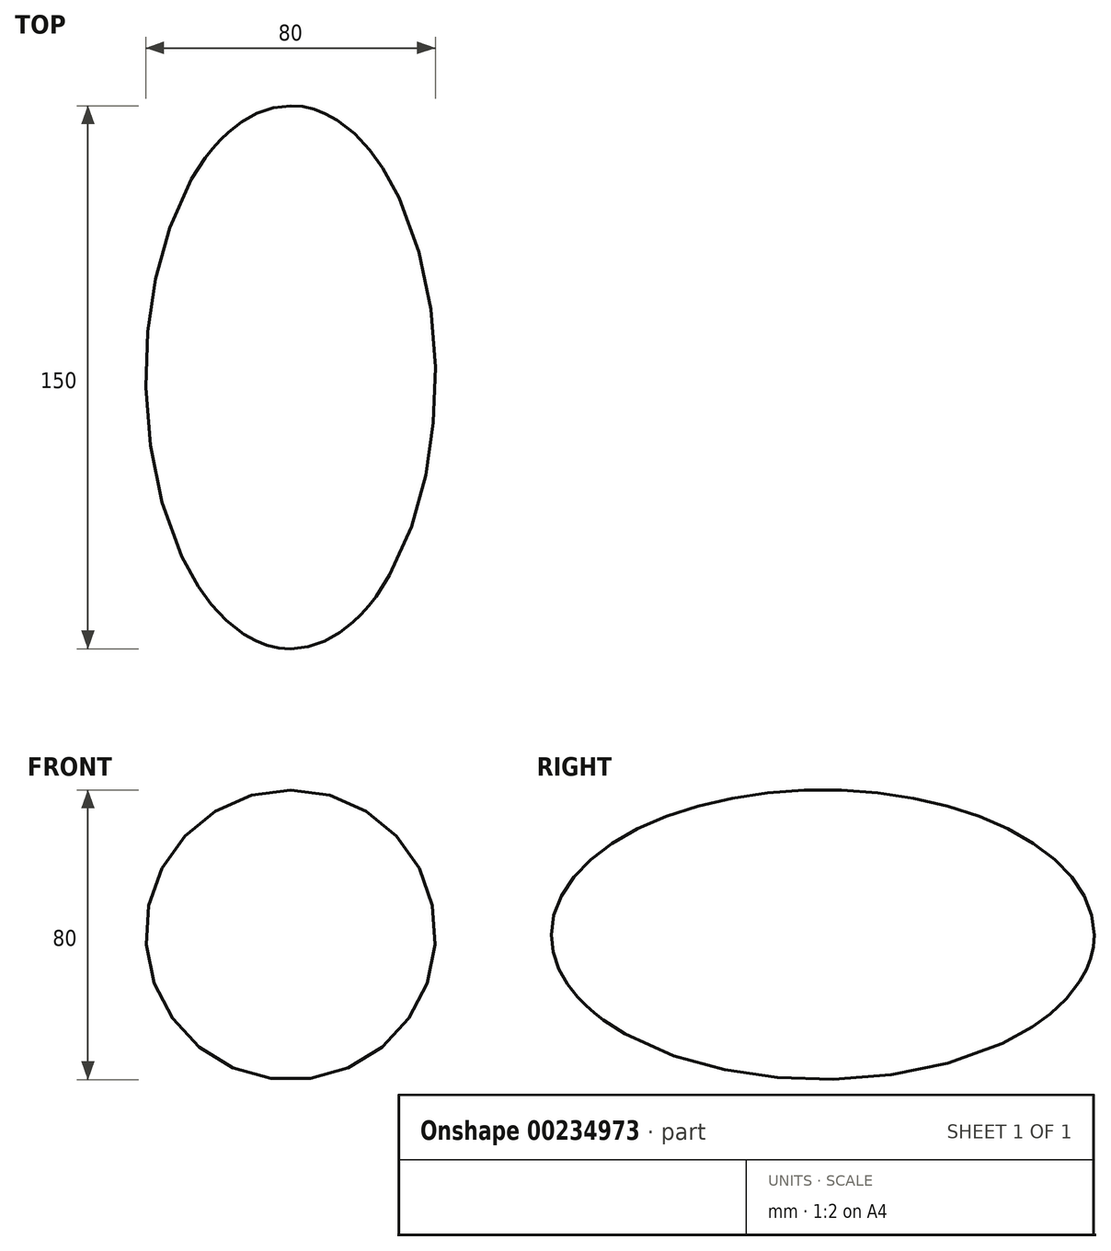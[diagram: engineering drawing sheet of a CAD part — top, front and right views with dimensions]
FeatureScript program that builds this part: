
annotation { "Feature Type Name" : "Feature", "Feature Type Description" : "" }
export const myFeature = defineFeature(function(context is Context, id is Id, definition is map)
    precondition{}
    {
        {
            var Q0;
            Q0=qCreatedBy(makeId("Right.planeOp"),FACE);
            var sketch = newSketch(context, id + "F0", { "sketchPlane" : qUnion([Q0])});
            skEllipticalArc(sketch, "E0", {});
            skLineSegment(sketch, "E1", {"start": v(75, 0) * mm, "end": v(-75, 0) * mm});
            const initialGuessF0  = {"E0": [0, 0, 1, 0, 0.075, 0.04, 0, 3.141592653589793]};
            skSetInitialGuess(sketch, initialGuessF0);
            skSolve(sketch);
        }
        {
            var Q0;
            Q0 = qSketchRegion(id + "F0", true);
            var Q1;
            Q1=sQuery(id+"F0.wireOp",EDGE,"E1");
            revolve(context, id + "F1", {"entities" : qUnion([Q0]), "axis" : qUnion([Q1]), "revolveType" : RevolveType.FULL});
        }
    });
